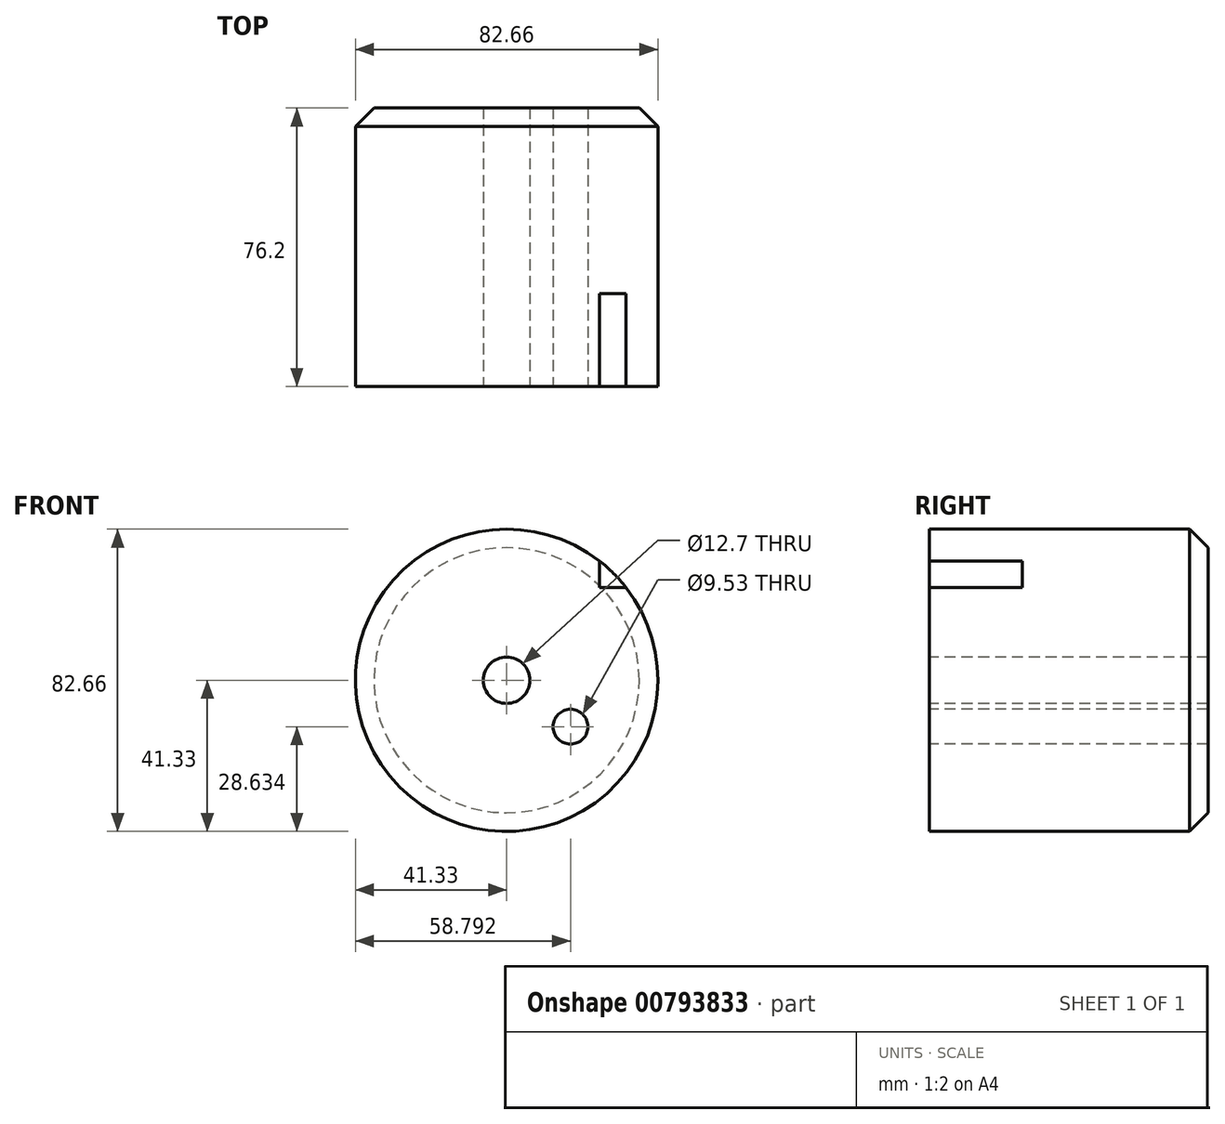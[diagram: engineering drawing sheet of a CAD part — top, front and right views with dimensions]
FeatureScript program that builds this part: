
annotation { "Feature Type Name" : "Feature", "Feature Type Description" : "" }
export const myFeature = defineFeature(function(context is Context, id is Id, definition is map)
    precondition{}
    {
        {
            var Q0;
            Q0=qCreatedBy(makeId("Front.planeOp"),FACE);
            var sketch = newSketch(context, id + "F0", { "sketchPlane" : qUnion([Q0])});
            skCircle(sketch, "E0", {"center": v(0, 0) * mm, "radius": 41.33 * mm});
            skSolve(sketch);
        }
        {
            var Q0;
            Q0=makeQuery(id+"F0.imprint","IMPRINT",FACE,{"disambiguationData":[TD([[makeQuery(id+"F0.imprint","IMPRINT",EDGE,{"derivedFrom":sQuery(id+"F0.wireOp",EDGE,"E0")}),1.0]])]});
            extrude(context, id + "F1", {"entities" : qUnion([Q0]), "depth" : 76.2 * mm, "offsetDistance" : 25.4 * mm});
        }
        {
            var Q0;
            Q0=makeQuery(id+"F1.opExtrude","CAP_FACE",FACE,{"disambiguationData":[OSD([sQuery(id+"F0.wireOp",EDGE,"E0")])],"isStart":false});
            var sketch = newSketch(context, id + "F2", { "sketchPlane" : qUnion([Q0])});
            skLineSegment(sketch, "E1.bottom", {"start": v(25.4, 50.8) * mm, "end": v(50.8, 50.8) * mm});
            skLineSegment(sketch, "E1.top", {"start": v(25.4, 25.4) * mm, "end": v(50.8, 25.4) * mm});
            skLineSegment(sketch, "E1.left", {"start": v(25.4, 50.8) * mm, "end": v(25.4, 25.4) * mm});
            skLineSegment(sketch, "E1.right", {"start": v(50.8, 50.8) * mm, "end": v(50.8, 25.4) * mm});
            skSolve(sketch);
        }
        {
            var Q0;
            Q0 = qSketchRegion(id + "F2", true);
            extrude(context, id + "F3", {"entities" : qUnion([Q0]), "operationType" : NewBodyOperationType.REMOVE, "oppositeDirection" : true, "depth" : 25.4 * mm, "offsetDistance" : 25.4 * mm});
        }
        {
            var Q0;
            Q0=makeQuery(id+"F1.opExtrude","CAP_EDGE",EDGE,{"disambiguationData":[OSD([sQuery(id+"F0.wireOp",EDGE,"E0")])],"isStart":true});
            chamfer(context, id + "F4", {"entities" : qUnion([Q0]), "width" : 5.08 * mm, "tangentPropagation" : true});
        }
        {
            var Q0;
            Q0=makeQuery(id+"F1.opExtrude","CAP_FACE",FACE,{"disambiguationData":[OSD([sQuery(id+"F0.wireOp",EDGE,"E0")])],"isStart":false});
            var sketch = newSketch(context, id + "F5", { "sketchPlane" : qUnion([Q0])});
            skPoint(sketch, "E2", {"position": v(0, 0) * mm});
            skSolve(sketch);
        }
        {
            var Q0;
            Q0=sQuery(id+"F5.wireOp",VERTEX,"E2");
            var Q1;
            Q1=makeQuery(id+"F1.opExtrude","SWEPT_BODY",BODY,{"disambiguationData":[OSD([sQuery(id+"F0.wireOp",EDGE,"E0")])]});
            hole(context, id + "F6", {"style" : HoleStyle.SIMPLE, "endStyle" : HoleEndStyle.THROUGH, "holeDiameter" : 12.7 * mm, "majorDiameter" : 6.35 * mm, "isTappedThrough" : true, "tappedDepth" : 12.7 * mm, "tapClearance" : 3, "locations" : qUnion([Q0]), "scope" : qUnion([Q1])});
        }
        {
            var Q0;
            Q0=makeQuery(id+"F1.opExtrude","CAP_FACE",FACE,{"disambiguationData":[OSD([sQuery(id+"F0.wireOp",EDGE,"E0")])],"isStart":false});
            var sketch = newSketch(context, id + "F7", { "sketchPlane" : qUnion([Q0])});
            skCircle(sketch, "E3", {"center": v(17.46, -12.7) * mm, "radius": 4.76 * mm});
            skSolve(sketch);
        }
        {
            var Q0;
            Q0=makeQuery(id+"F7.imprint","IMPRINT",FACE,{"disambiguationData":[TD([[makeQuery(id+"F7.imprint","IMPRINT",EDGE,{"derivedFrom":sQuery(id+"F7.wireOp",EDGE,"E3")}),1.0]])]});
            extrude(context, id + "F8", {"entities" : qUnion([Q0]), "operationType" : NewBodyOperationType.REMOVE, "endBound" : BoundingType.UP_TO_NEXT, "oppositeDirection" : true, "depth" : 25.4 * mm, "offsetDistance" : 25.4 * mm});
        }
    });
